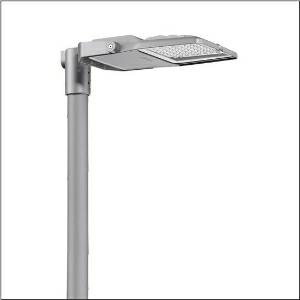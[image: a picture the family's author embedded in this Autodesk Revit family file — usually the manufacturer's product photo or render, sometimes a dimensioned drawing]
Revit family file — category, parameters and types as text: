
# Revit family: floodlight_fl_21_iq_mini___pl43_5xa7771d4a3a_2bc1
name_source: partatom
category: Lighting Fixtures
units: mm (PartAtom-declared; Revit-internal decimal feet)

## family parameters
Cut with Voids When Loaded = No
Host = Face
Light Source = No
Part Type = Normal
Room Calculation Point = No
Round Connector Dimension = Use Diameter
Shared = No

## types (1)
- --- (1 x LED, 19090 lm, 143 W, 4000K)
    Apparent Load = 143 VA
    CIE Flux Codes = 27 78 99 100 100
    Color Rendering = 70
    Color Temperature = 4000K
    Default Elevation = 1800 mm
    Description = Floodlight FL 21 iQ mini, floodlight, primary light control with lens, of PMMA, primary optical cover: protective disc, of toughened safety glass, transparent, light distribution: PL43, light emission: direct distribution, installation type: surface-mounted, LED, High Power LED, rated luminous flux: 19.090lm, luminous efficacy: 134lm/W, light colour: 740, colour temperature: 4000K, control gear: iQ Comfort/DALI, control: Auto-Match, Temp-Guard, Lumen-Switch, Night-Set, Smart-Wire, Light-Fading, Desk-Remote (wireless, voltage-free reading and setting of iQ features in the workshop via application-optimized NFC function/RFID function), optimised constant luminous flux control (CLO 2.0), with terminal, 6-pole, mains connection: 220..240V, AC, 50/60Hz, start of lifetime: 143W, end of service life: 152W, reduction: 61W, luminaire housing, of diecast aluminium, powder-coated, Siteco® metallic grey (DB 702S), corrosivity category C5 mid according to DIN EN ISO 12944, suitable for swimming pools, chlorine-resistant, sealing non-destructively replaceable, please order mast flange separately, mast bracket, of steel, galvanised, powder-coated, Siteco® metallic grey (DB 702S), protection rating (complete): IP66, insulation class (complete): insulation class II (safety insulation), certification: CE, ENEC, VDE, protection symbol: D, impact resistance: IK08, permissible operating ambient temperature: -40..+40°C, permissible operating ambient temperature for outdoor applications: -40..+50°C, standard: DIN EN 12944, LABS conformity tested according to VDMA 24364:2018-05, packaging unit: 1 piece

Light Distribution: PL43
    Height = 70 mm
    Lamp = 1 x LED
    Lamp Light Flux = 19090 lm
    Lamp Power = 143 W
    Lamp count = 1
    Length = 485 mm
    Luminous efficacy = 133 lm/W
    Manufacturer = Siteco
    ModVariant = No
    Model = 5XA7771D4A3A
    Number of Poles = 1
    OnlyDefault = Yes
    Power Factor = 1
    Product Name = Floodlight FL 21 iQ mini | PL43
    Product group = floodlight | pylon annexe
    ProductGroupID = 6201
    Protection Class = Protection class II
    Protection Degree = IP 66
    RLX_Detail_Level = 1
    RLX_Emergency_Light_Flux = 0 lm
    RLX_Emergency_Type = 0
    RLX_Emergency_Type_DB = No
    RlxData = <blob elided: 101637 chars, md5=b126c3c5>
    Socket = socket
    Standby Power = 0 W
    System Light Flux = 19090 lm
    System Power = 143 W
    Type Comments = factory setting: luminous flux: 100 % | dim-lin: 254 | 730 mA
    Type Image = l_1007125.jpg
    URL = http://relux.com
    VarID = @adj_183203
    Voltage = 0 V
    Weight = 0.00 kg
    Width = 337 mm

## geometry (parser evidence)
native form markers: Blend x4, Sweep x11
no freeform markers — native parametric forms only
